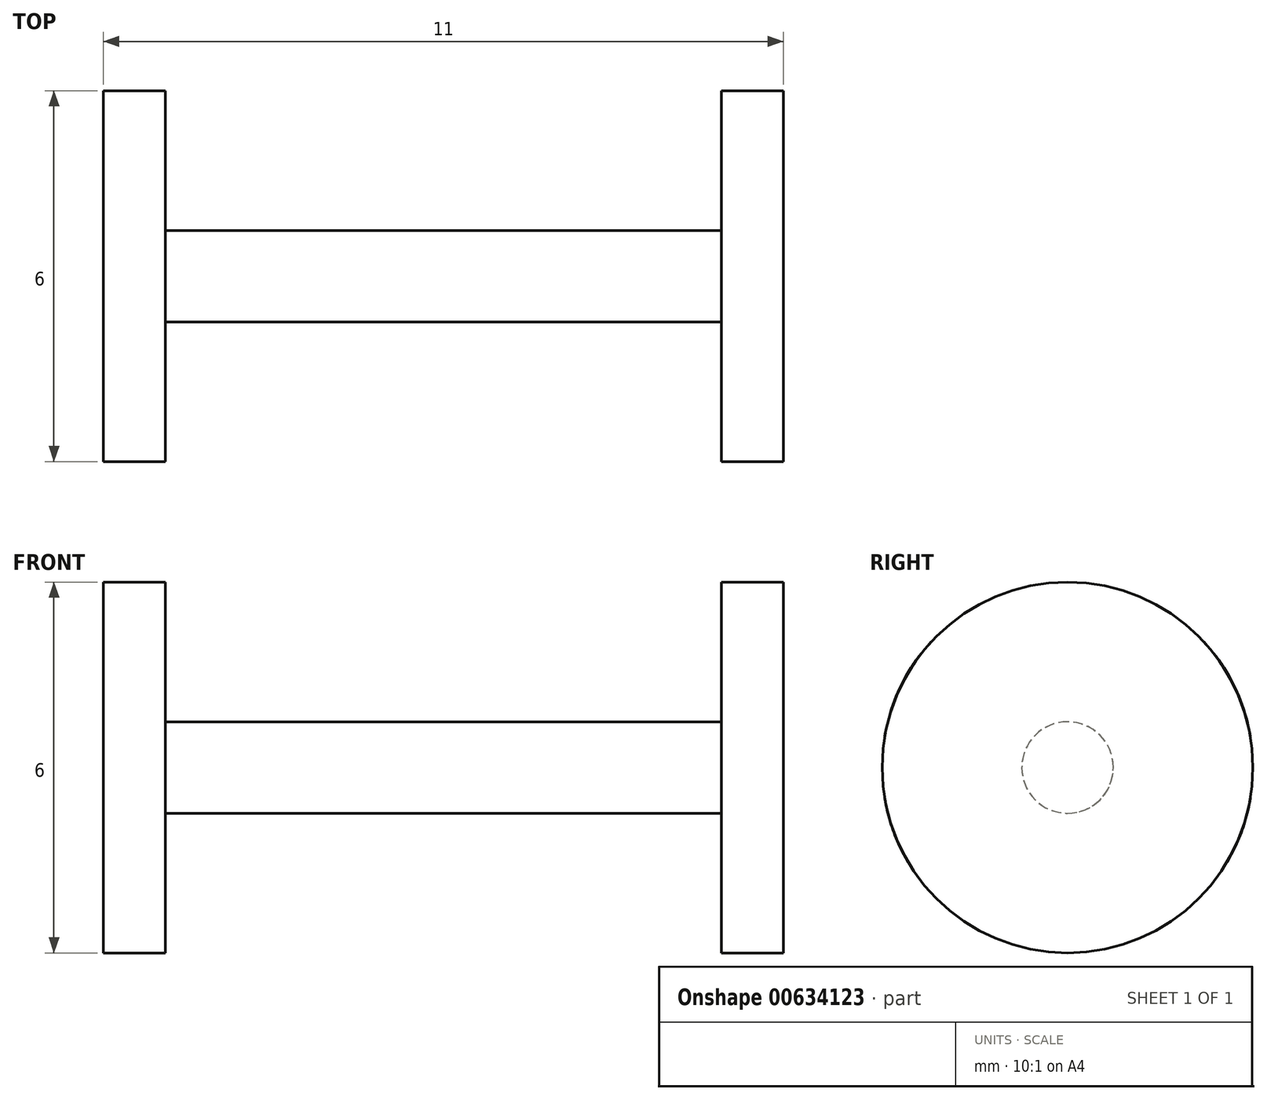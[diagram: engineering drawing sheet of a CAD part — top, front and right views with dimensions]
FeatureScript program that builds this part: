
annotation { "Feature Type Name" : "Feature", "Feature Type Description" : "" }
export const myFeature = defineFeature(function(context is Context, id is Id, definition is map)
    precondition{}
    {
        {
            var Q0;
            Q0=qCreatedBy(makeId("Front.planeOp"),FACE);
            var sketch = newSketch(context, id + "F0", { "sketchPlane" : qUnion([Q0])});
            skLineSegment(sketch, "E0.bottom", {"start": v(-15, 40) * mm, "end": v(15, 40) * mm});
            skLineSegment(sketch, "E0.top", {"start": v(-12, 0) * mm, "end": v(12, 0) * mm});
            skLineSegment(sketch, "E0.left", {"start": v(-15, 40) * mm, "end": v(-15, 37) * mm});
            skLineSegment(sketch, "E0.right", {"start": v(15, 37) * mm, "end": v(15, 3) * mm});
            skLineSegment(sketch, "E1.0", {"start": v(-15, 37) * mm, "end": v(3, 37) * mm});
            skLineSegment(sketch, "E1.1", {"start": v(-12, 6) * mm, "end": v(-12, 6) * mm});
            skLineSegment(sketch, "E1.2", {"start": v(-9, 3) * mm, "end": v(9, 3) * mm});
            skLineSegment(sketch, "E1.3", {"start": v(12, 29.6) * mm, "end": v(12, 6) * mm});
            skLineSegment(sketch, "E2.0", {"start": v(-15, 6) * mm, "end": v(-12, 6) * mm});
            skLineSegment(sketch, "E3", {"start": v(12, 40) * mm, "end": v(7.5, 40) * mm, "construction": true});
            skLineSegment(sketch, "E4", {"start": v(7, 34.8) * mm, "end": v(7, 40) * mm, "construction": true});
            skArc(sketch, "E5", {"start": v(7, 40) * mm, "mid": v(6.75, 29.6) * mm, "end": v(7.5, 39.98) * mm});
            skLineSegment(sketch, "E6.trimOffspring", {"start": v(-15, 6) * mm, "end": v(-15, 3) * mm});
            skPoint(sketch, "E7.orphan", {"position": v(5, 29.7) * mm});
            skPoint(sketch, "E8.visualSharp", {"position": v(15, 40) * mm});
            skArc(sketch, "E8.filletArc", {"start": v(15, 37) * mm, "mid": v(14.12, 39.12) * mm, "end": v(12, 40) * mm});
            skPoint(sketch, "E9.visualSharp", {"position": v(15, 0) * mm});
            skArc(sketch, "E9.filletArc", {"start": v(12, 0) * mm, "mid": v(14.12, 0.88) * mm, "end": v(15, 3) * mm});
            skArc(sketch, "E10.filletArc", {"start": v(9, 3) * mm, "mid": v(11.12, 3.88) * mm, "end": v(12, 6) * mm});
            skPoint(sketch, "E11.visualSharp", {"position": v(-12, 3) * mm});
            skArc(sketch, "E11.filletArc", {"start": v(-12, 6) * mm, "mid": v(-11.12, 3.88) * mm, "end": v(-9, 3) * mm});
            skPoint(sketch, "E12.visualSharp", {"position": v(-15, 0) * mm});
            skArc(sketch, "E12.filletArc", {"start": v(-15, 3) * mm, "mid": v(-14.12, 0.88) * mm, "end": v(-12, 0) * mm});
            skLineSegment(sketch, "E13.0", {"start": v(6.5, 34.8) * mm, "end": v(6.5, 39.8) * mm});
            skLineSegment(sketch, "E14.0", {"start": v(7.5, 34.8) * mm, "end": v(7.5, 40) * mm});
            skLineSegment(sketch, "E15", {"start": v(-15, 6) * mm, "end": v(-15, 16) * mm});
            skLineSegment(sketch, "E16", {"start": v(-15, 16) * mm, "end": v(-12, 16) * mm});
            skLineSegment(sketch, "E17", {"start": v(-12, 16) * mm, "end": v(-12, 6) * mm});
            skLineSegment(sketch, "E18", {"start": v(6.75, 29.6) * mm, "end": v(12, 29.6) * mm});
            skSolve(sketch);
        }
        {
            var Q0;
            Q0=qCreatedBy(makeId("Front.planeOp"),FACE);
            var sketch = newSketch(context, id + "F1", { "sketchPlane" : qUnion([Q0])});
            skLineSegment(sketch, "E19.1.1", {"start": v(7.5, 40) * mm, "end": v(-15, 40) * mm});
            skLineSegment(sketch, "E19.1.2", {"start": v(-15, 40) * mm, "end": v(-15, 37) * mm});
            skArc(sketch, "E19.2.8", {"start": v(-15, 3) * mm, "mid": v(-14.12, 0.88) * mm, "end": v(-12, 0) * mm, "construction": true});
            skLineSegment(sketch, "E19.2.9", {"start": v(-12, 0) * mm, "end": v(-5, 0) * mm});
            skLineSegment(sketch, "E19.2.13", {"start": v(17, 40) * mm, "end": v(8.5, 40) * mm});
            skLineSegment(sketch, "E19.3.0", {"start": v(-15, 18) * mm, "end": v(-15, 7.7) * mm});
            skPoint(sketch, "E20.2", {"position": v(6.5, 37.3) * mm});
            skPoint(sketch, "E21.orphan", {"position": v(6.5, 39.8) * mm});
            skPoint(sketch, "E19.0.2.end.orphan", {"position": v(7, 40) * mm});
            skPoint(sketch, "E22.orphan", {"position": v(12, 29.6) * mm});
            skPoint(sketch, "E23.orphan", {"position": v(7.5, 34.8) * mm});
            skPoint(sketch, "E20.0.start.orphan", {"position": v(6.5, 34.8) * mm});
            skLineSegment(sketch, "E24", {"start": v(-15, 37) * mm, "end": v(-15, 31) * mm});
            skLineSegment(sketch, "E25", {"start": v(0, 0) * mm, "end": v(0, 15) * mm, "construction": true});
            skLineSegment(sketch, "E26", {"start": v(7.5, 40) * mm, "end": v(7.5, 37.97) * mm});
            skLineSegment(sketch, "E27", {"start": v(8.5, 40) * mm, "end": v(8.5, 37.97) * mm});
            skLineSegment(sketch, "E28", {"start": v(15, 32.5) * mm, "end": v(8, 32.5) * mm, "construction": true});
            skPoint(sketch, "E29.orphan", {"position": v(7.6, 39) * mm});
            skLineSegment(sketch, "E30", {"start": v(8, 39) * mm, "end": v(8, 32.5) * mm, "construction": true});
            skPoint(sketch, "E19.3.3.end.orphan", {"position": v(-15, 16) * mm});
            skPoint(sketch, "E19.3.3.start.orphan", {"position": v(-12, 16) * mm});
            skLineSegment(sketch, "E31", {"start": v(-15, 3) * mm, "end": v(-15, 0) * mm});
            skLineSegment(sketch, "E32", {"start": v(-12, 0) * mm, "end": v(-15, 0) * mm});
            skLineSegment(sketch, "E33", {"start": v(-15, 40) * mm, "end": v(-15, 31) * mm, "construction": true});
            skLineSegment(sketch, "E34", {"start": v(-15, 40) * mm, "end": v(-15, 31) * mm});
            skLineSegment(sketch, "E35.trimOffspring", {"start": v(-15, 31) * mm, "end": v(-15, 26) * mm});
            skLineSegment(sketch, "E36.trimOffspring", {"start": v(-15, 29) * mm, "end": v(-15, 24) * mm});
            skPoint(sketch, "E37.orphan", {"position": v(12, 40) * mm});
            skPoint(sketch, "E38.orphan", {"position": v(12, 0) * mm});
            skLineSegment(sketch, "E39.0", {"start": v(13.1, 38) * mm, "end": v(13.1, 38) * mm});
            skLineSegment(sketch, "E40.1", {"start": v(-13, 2) * mm, "end": v(-11, 2) * mm, "construction": true});
            skLineSegment(sketch, "E41.0", {"start": v(-13, 38) * mm, "end": v(-13, 34) * mm});
            skArc(sketch, "E42", {"start": v(13.32, 33.87) * mm, "mid": v(11.56, 36.69) * mm, "end": v(8.5, 37.97) * mm});
            skLineSegment(sketch, "E43.0", {"start": v(29.42, 20) * mm, "end": v(-7, 20) * mm, "construction": true});
            skLineSegment(sketch, "E44.trimOffspring", {"start": v(-13, 0.17) * mm, "end": v(-13, 0) * mm});
            skArc(sketch, "E45.0", {"start": v(2.9, 38) * mm, "mid": v(3.81, 26.3) * mm, "end": v(15, 29.84) * mm});
            skLineSegment(sketch, "E46.trimOffspring", {"start": v(2.9, 38) * mm, "end": v(-13, 38) * mm});
            skLineSegment(sketch, "E47.trimOffspring", {"start": v(13.32, 33.87) * mm, "end": v(13.43, 31.7) * mm});
            skArc(sketch, "E48.trimOffspring", {"start": v(13.1, 38) * mm, "mid": v(13.1, 38) * mm, "end": v(13.1, 38) * mm});
            skArc(sketch, "E49.trimOffspring", {"start": v(7.5, 37.97) * mm, "mid": v(4.01, 28.73) * mm, "end": v(13.43, 31.7) * mm});
            skPoint(sketch, "E50.orphan", {"position": v(7.5, 39) * mm});
            skPoint(sketch, "E51.start.orphan", {"position": v(8.5, 39) * mm});
            skLineSegment(sketch, "E52.0", {"start": v(8, 0) * mm, "end": v(8, 13.5) * mm});
            skLineSegment(sketch, "E53.0", {"start": v(-5, 0) * mm, "end": v(-5, 13.5) * mm});
            skLineSegment(sketch, "E54.0", {"start": v(16.47, 12) * mm, "end": v(14.46, 12) * mm, "construction": true});
            skLineSegment(sketch, "E55.trimOffspring", {"start": v(12.84, 12) * mm, "end": v(10, 12) * mm});
            skLineSegment(sketch, "E56.0", {"start": v(1.5, 0) * mm, "end": v(1.5, 20) * mm, "construction": true});
            skLineSegment(sketch, "E57", {"start": v(1.5, 20) * mm, "end": v(-9.16, 15.5) * mm});
            skLineSegment(sketch, "E58", {"start": v(1.5, 20) * mm, "end": v(10.84, 15.5) * mm});
            skLineSegment(sketch, "E59.0", {"start": v(-9.16, 13.5) * mm, "end": v(-5, 13.5) * mm});
            skLineSegment(sketch, "E60", {"start": v(-9.16, 15.5) * mm, "end": v(-9.16, 13.5) * mm});
            skLineSegment(sketch, "E61", {"start": v(10.84, 15.5) * mm, "end": v(10.84, 13.5) * mm});
            skLineSegment(sketch, "E62.trimOffspring", {"start": v(8, 13.5) * mm, "end": v(10.84, 13.5) * mm});
            skLineSegment(sketch, "E63.trimOffspring", {"start": v(10, 2) * mm, "end": v(15, 2) * mm});
            skLineSegment(sketch, "E64.trimOffspring", {"start": v(8, 0) * mm, "end": v(17, 0) * mm});
            skLineSegment(sketch, "E65.0", {"start": v(10, 2) * mm, "end": v(10, 12) * mm});
            skLineSegment(sketch, "E66.0", {"start": v(1.55, 22.2) * mm, "end": v(-7, 18.58) * mm});
            skLineSegment(sketch, "E66.1", {"start": v(1.55, 22.2) * mm, "end": v(12.84, 16.75) * mm});
            skLineSegment(sketch, "E67.0", {"start": v(-11.16, 16.82) * mm, "end": v(-11.16, 15.5) * mm});
            skLineSegment(sketch, "E68.0", {"start": v(-13, 11.5) * mm, "end": v(-7, 11.5) * mm});
            skLineSegment(sketch, "E69", {"start": v(-11.16, 15.5) * mm, "end": v(-11.16, 13.5) * mm});
            skLineSegment(sketch, "E70.0", {"start": v(12.84, 16.75) * mm, "end": v(12.84, 12) * mm});
            skLineSegment(sketch, "E71.0", {"start": v(-13, 6.7) * mm, "end": v(-7, 6.7) * mm, "construction": true});
            skLineSegment(sketch, "E72.0", {"start": v(-15, 7.7) * mm, "end": v(-13, 7.7) * mm});
            skLineSegment(sketch, "E73.0", {"start": v(-15, 5.7) * mm, "end": v(-11, 5.7) * mm});
            skLineSegment(sketch, "E74.0", {"start": v(-15, 3.7) * mm, "end": v(-13, 3.7) * mm, "construction": true});
            skLineSegment(sketch, "E75.trimOffspring", {"start": v(-15, 5.7) * mm, "end": v(-15, 3) * mm});
            skLineSegment(sketch, "E76.trimOffspring", {"start": v(-13, 3.7) * mm, "end": v(-13, 2) * mm, "construction": true});
            skLineSegment(sketch, "E77.trimOffspring", {"start": v(-11, 5.7) * mm, "end": v(-11, 2) * mm});
            skLineSegment(sketch, "E78.0", {"start": v(-13, 13.5) * mm, "end": v(-11.16, 13.5) * mm});
            skLineSegment(sketch, "E79.trimOffspring", {"start": v(-9.16, 13.5) * mm, "end": v(-7, 13.5) * mm});
            skLineSegment(sketch, "E80.trimOffspring", {"start": v(-13, 11.5) * mm, "end": v(-13, 7.7) * mm});
            skLineSegment(sketch, "E81.0", {"start": v(-7, 11.5) * mm, "end": v(-7, 3.7) * mm});
            skLineSegment(sketch, "E82.trimOffspring", {"start": v(-11, 3.7) * mm, "end": v(-7, 3.7) * mm});
            skLineSegment(sketch, "E83.0", {"start": v(17, 40) * mm, "end": v(17, 0) * mm});
            skPoint(sketch, "E84.orphan", {"position": v(17.1, 0) * mm});
            skLineSegment(sketch, "E85.trimOffspring", {"start": v(15, 29.84) * mm, "end": v(15, 2) * mm});
            skPoint(sketch, "E86.start.orphan", {"position": v(15, 40) * mm});
            skLineSegment(sketch, "E87", {"start": v(-13, 13.5) * mm, "end": v(-13, 18) * mm});
            skLineSegment(sketch, "E88.trimOffspring", {"start": v(-15, 22) * mm, "end": v(-15, 21.16) * mm, "construction": true});
            skLineSegment(sketch, "E89.trimOffspring", {"start": v(-15, 22) * mm, "end": v(-15, 18) * mm});
            skPoint(sketch, "E90.start.orphan", {"position": v(-12, 28) * mm});
            skPoint(sketch, "E91.orphan", {"position": v(-12, 29) * mm});
            skLineSegment(sketch, "E92.0", {"start": v(-9, 26) * mm, "end": v(-11, 26) * mm});
            skLineSegment(sketch, "E93.0", {"start": v(-11, 24) * mm, "end": v(-13, 24) * mm});
            skLineSegment(sketch, "E94", {"start": v(-9, 20) * mm, "end": v(-9, 26) * mm});
            skLineSegment(sketch, "E95.0", {"start": v(-11, 20) * mm, "end": v(-11, 22) * mm});
            skLineSegment(sketch, "E96.trimOffspring", {"start": v(-11, 24) * mm, "end": v(-11, 26) * mm});
            skLineSegment(sketch, "E97.trimOffspring", {"start": v(-13, 28) * mm, "end": v(-13, 34) * mm});
            skLineSegment(sketch, "E98", {"start": v(-15, 22) * mm, "end": v(-11, 22) * mm});
            skLineSegment(sketch, "E99", {"start": v(-13, 24) * mm, "end": v(-15, 24) * mm});
            skLineSegment(sketch, "E100.0", {"start": v(-7, 18.58) * mm, "end": v(-7, 28) * mm});
            skLineSegment(sketch, "E101.0", {"start": v(-13, 18) * mm, "end": v(-8.36, 18) * mm});
            skLineSegment(sketch, "E102.trimOffspring", {"start": v(-8.36, 18) * mm, "end": v(-11.16, 16.82) * mm});
            skLineSegment(sketch, "E103.0", {"start": v(-11, 20) * mm, "end": v(-9, 20) * mm});
            skLineSegment(sketch, "E104.0", {"start": v(-7, 28) * mm, "end": v(-13, 28) * mm});
            skSolve(sketch);
        }
        {
            var Q0;
            Q0=qSketchRegion(id+"F1",true);
            extrude(context, id + "F2", {"entities" : qUnion([Q0]), "oppositeDirection" : true, "depth" : 1910 * mm, "offsetDistance" : 25 * mm});
        }
        {
            var Q0;
            Q0=makeQuery(id+"F1.imprint","IMPRINT",FACE,{"disambiguationData":[TD([[makeQuery(id+"F1.imprint","IMPRINT",EDGE,{"derivedFrom":sQuery(id+"F1.wireOp",EDGE,"E19.1.1")}),1.0]])]});
            var sketch = newSketch(context, id + "F3", { "sketchPlane" : qUnion([Q0])});
            skLineSegment(sketch, "E105.0", {"start": v(-13.5, 18) * mm, "end": v(-13.5, -0.51) * mm});
            skSolve(sketch);
        }
        {
            var Q0;
            Q0=makeQuery(id+"F3.imprint","IMPRINT",FACE,{"disambiguationData":[TD([[makeQuery(id+"F3.imprint","IMPRINT",EDGE,{"derivedFrom":makeQuery(id+"F1.imprint","IMPRINT",EDGE,{"derivedFrom":sQuery(id+"F1.wireOp",EDGE,"E19.1.1")})}),1.0]])]});
            var sketch = newSketch(context, id + "F4", { "sketchPlane" : qUnion([Q0])});
            skLineSegment(sketch, "E106.0", {"start": v(-17, 40) * mm, "end": v(-25.5, 40) * mm});
            skLineSegment(sketch, "E107.0", {"start": v(-49.1, 40) * mm, "end": v(-49.1, 18) * mm});
            skLineSegment(sketch, "E108.0", {"start": v(-17, 40) * mm, "end": v(-17, 18) * mm});
            skPoint(sketch, "E109.orphan", {"position": v(7.5, 40) * mm});
            skLineSegment(sketch, "E110.1", {"start": v(-19, 29.83) * mm, "end": v(-19, 20) * mm});
            skLineSegment(sketch, "E110.3", {"start": v(-47.1, 38) * mm, "end": v(-47.1, 20) * mm});
            skArc(sketch, "E111.0", {"start": v(7.5, 37.97) * mm, "mid": v(4.01, 28.73) * mm, "end": v(13.43, 31.7) * mm, "construction": true});
            skLineSegment(sketch, "E112.0", {"start": v(17, 40) * mm, "end": v(8.5, 40) * mm});
            skLineSegment(sketch, "E113.0", {"start": v(7.5, 40) * mm, "end": v(-15, 40) * mm});
            skLineSegment(sketch, "E114.0", {"start": v(-26.6, 40) * mm, "end": v(-26.6, 37.97) * mm});
            skLineSegment(sketch, "E115.0", {"start": v(-25.5, 40) * mm, "end": v(-25.5, 37.98) * mm});
            skLineSegment(sketch, "E116.0", {"start": v(-7, 18.58) * mm, "end": v(-7, 28) * mm});
            skLineSegment(sketch, "E117", {"start": v(-47.1, 23.29) * mm, "end": v(15, 23.29) * mm, "construction": true});
            skPoint(sketch, "E118.orphan", {"position": v(-7, 23.29) * mm});
            skLineSegment(sketch, "E119", {"start": v(8, 32.5) * mm, "end": v(2.5, 32.5) * mm});
            skLineSegment(sketch, "E120.0", {"start": v(8, 39) * mm, "end": v(8, 32.5) * mm});
            skLineSegment(sketch, "E120.1", {"start": v(17, 40) * mm, "end": v(17, 0) * mm});
            skLineSegment(sketch, "E121.trimOffspring", {"start": v(-17, 32.5) * mm, "end": v(-26, 32.5) * mm, "construction": true});
            skArc(sketch, "E122", {"start": v(-26.6, 37.97) * mm, "mid": v(-25.95, 27.01) * mm, "end": v(-25.5, 37.98) * mm});
            skArc(sketch, "E123.0", {"start": v(-31.1, 38) * mm, "mid": v(-30.2, 26.3) * mm, "end": v(-19, 29.83) * mm});
            skLineSegment(sketch, "E124.trimOffspring", {"start": v(-26.6, 40) * mm, "end": v(-49.1, 40) * mm});
            skLineSegment(sketch, "E125.trimOffspring", {"start": v(-26.6, 27.05) * mm, "end": v(-26.6, 20) * mm, "construction": true});
            skLineSegment(sketch, "E126.trimOffspring", {"start": v(-25.5, 27.04) * mm, "end": v(-25.5, 20) * mm, "construction": true});
            skLineSegment(sketch, "E127.trimOffspring", {"start": v(-31.1, 38) * mm, "end": v(-47.1, 38) * mm});
            skLineSegment(sketch, "E128.0", {"start": v(-49.1, 18) * mm, "end": v(-17, 18) * mm});
            skPoint(sketch, "E129.orphan", {"position": v(-8.36, 18) * mm});
            skPoint(sketch, "E130.orphan", {"position": v(-13, 18) * mm});
            skLineSegment(sketch, "E131.0", {"start": v(-47.1, 20) * mm, "end": v(-19, 20) * mm});
            skSolve(sketch);
        }
        {
            var Q0;
            Q0=makeQuery(id+"F1.imprint","IMPRINT",FACE,{"disambiguationData":[TD([[makeQuery(id+"F1.imprint","IMPRINT",EDGE,{"derivedFrom":sQuery(id+"F1.wireOp",EDGE,"E19.1.1")}),1.0]])]});
            var sketch = newSketch(context, id + "F5", { "sketchPlane" : qUnion([Q0])});
            skArc(sketch, "E132.0", {"start": v(7.5, 37.97) * mm, "mid": v(4.01, 28.73) * mm, "end": v(13.43, 31.7) * mm, "construction": true});
            skArc(sketch, "E132.1", {"start": v(13.32, 33.87) * mm, "mid": v(11.56, 36.69) * mm, "end": v(8.5, 37.97) * mm, "construction": true});
            skLineSegment(sketch, "E132.2", {"start": v(7.5, 40) * mm, "end": v(-15, 40) * mm});
            skArc(sketch, "E132.3", {"start": v(-26.6, 37.97) * mm, "mid": v(-25.95, 27.01) * mm, "end": v(-25.5, 37.98) * mm, "construction": true});
            skLineSegment(sketch, "E133.0", {"start": v(-15, 40) * mm, "end": v(-25.5, 40) * mm});
            skPoint(sketch, "E134.orphan", {"position": v(-26.6, 40) * mm});
            skLineSegment(sketch, "E135.0", {"start": v(7.5, 40) * mm, "end": v(7.5, 37.37) * mm});
            skLineSegment(sketch, "E135.1", {"start": v(8.5, 40) * mm, "end": v(8.5, 37.37) * mm});
            skLineSegment(sketch, "E135.2", {"start": v(-25.5, 40) * mm, "end": v(-25.5, 37.37) * mm});
            skLineSegment(sketch, "E135.3", {"start": v(-26.6, 40) * mm, "end": v(-26.6, 37.36) * mm});
            skPoint(sketch, "E135.4", {"position": v(-25.5, 38.99) * mm});
            skLineSegment(sketch, "E136", {"start": v(-49.1, 40) * mm, "end": v(-216.5, 40) * mm});
            skLineSegment(sketch, "E137.0", {"start": v(8.5, 41) * mm, "end": v(-216.5, 41) * mm});
            skLineSegment(sketch, "E138", {"start": v(8.5, 40) * mm, "end": v(8.5, 41) * mm});
            skLineSegment(sketch, "E139", {"start": v(-216.5, 41) * mm, "end": v(-216.5, 40) * mm, "construction": true});
            skArc(sketch, "E140.0", {"start": v(7.5, 37.37) * mm, "mid": v(4.47, 29.12) * mm, "end": v(12.84, 31.8) * mm});
            skArc(sketch, "E141.0", {"start": v(12.74, 33.72) * mm, "mid": v(11.2, 36.21) * mm, "end": v(8.5, 37.37) * mm});
            skArc(sketch, "E142", {"start": v(12.74, 33.72) * mm, "mid": v(12.88, 32.76) * mm, "end": v(12.84, 31.8) * mm});
            skPoint(sketch, "E143.orphan", {"position": v(7.5, 37.97) * mm});
            skPoint(sketch, "E144.orphan", {"position": v(8.5, 37.97) * mm});
            skArc(sketch, "E145.0", {"start": v(-26.6, 37.36) * mm, "mid": v(-25.95, 27.61) * mm, "end": v(-25.5, 37.37) * mm});
            skPoint(sketch, "E146.orphan", {"position": v(-26.6, 37.97) * mm});
            skPoint(sketch, "E147.orphan", {"position": v(-25.5, 37.98) * mm});
            skLineSegment(sketch, "E148.trimOffspring", {"start": v(-26.6, 40) * mm, "end": v(-49.1, 40) * mm});
            skSolve(sketch);
        }
        {
            var Q0;
            {var subQ7=sQuery(id+"F5.wireOp",EDGE,"E132.2");Q0=makeQuery(id+"F5.imprint","IMPRINT",FACE,{"disambiguationData":[TD([[makeQuery(id+"F5.imprint","IMPRINT",EDGE,{"derivedFrom":subQ7}),1.0]])]});}
            var sketch = newSketch(context, id + "F6", { "sketchPlane" : qUnion([Q0])});
            skLineSegment(sketch, "E149.0", {"start": v(-13, 11.5) * mm, "end": v(-7, 11.5) * mm});
            skLineSegment(sketch, "E149.1", {"start": v(-7, 11.5) * mm, "end": v(-7, 3.7) * mm});
            skLineSegment(sketch, "E149.2", {"start": v(-11, 3.7) * mm, "end": v(-7, 3.7) * mm});
            skLineSegment(sketch, "E149.3", {"start": v(-11, 5.7) * mm, "end": v(-11, 3.7) * mm});
            skLineSegment(sketch, "E149.4", {"start": v(-15, 5.7) * mm, "end": v(-11, 5.7) * mm});
            skLineSegment(sketch, "E149.5", {"start": v(-15, 7.7) * mm, "end": v(-13, 7.7) * mm});
            skLineSegment(sketch, "E149.6", {"start": v(-13, 11.5) * mm, "end": v(-13, 7.7) * mm});
            skPoint(sketch, "E150.orphan", {"position": v(-11, 2) * mm});
            skLineSegment(sketch, "E151.0", {"start": v(-15, 18) * mm, "end": v(-15, 7.7) * mm});
            skLineSegment(sketch, "E151.1", {"start": v(-15, 3) * mm, "end": v(-15, 0) * mm});
            skLineSegment(sketch, "E151.2", {"start": v(-15, 5.7) * mm, "end": v(-15, 3) * mm});
            skLineSegment(sketch, "E152.0", {"start": v(-17, 18) * mm, "end": v(-17, 15.63) * mm});
            skLineSegment(sketch, "E153.0", {"start": v(-17, 3) * mm, "end": v(-17, 0) * mm});
            skLineSegment(sketch, "E154", {"start": v(-17, 18) * mm, "end": v(-15, 18) * mm});
            skLineSegment(sketch, "E155", {"start": v(-17, 0) * mm, "end": v(-15, 0) * mm});
            skLineSegment(sketch, "E156", {"start": v(-17, 3) * mm, "end": v(-26.75, 3) * mm});
            skLineSegment(sketch, "E157", {"start": v(-26.75, 3) * mm, "end": v(-26.75, 15.63) * mm});
            skLineSegment(sketch, "E158", {"start": v(-26.75, 15.63) * mm, "end": v(-17, 15.63) * mm});
            skSolve(sketch);
        }
        {
            var Q0;
            Q0=makeQuery(id+"F2.opExtrude","CAP_FACE",FACE,{"disambiguationData":[OSD([sQuery(id+"F1.wireOp",EDGE,"E19.1.1"),sQuery(id+"F1.wireOp",EDGE,"E19.2.9"),sQuery(id+"F1.wireOp",EDGE,"E19.2.13"),sQuery(id+"F1.wireOp",EDGE,"E19.3.0"),sQuery(id+"F1.wireOp",EDGE,"E26"),sQuery(id+"F1.wireOp",EDGE,"E27"),sQuery(id+"F1.wireOp",EDGE,"E31"),sQuery(id+"F1.wireOp",EDGE,"E32"),sQuery(id+"F1.wireOp",EDGE,"E34"),sQuery(id+"F1.wireOp",EDGE,"E35.trimOffspring"),sQuery(id+"F1.wireOp",EDGE,"E36.trimOffspring"),sQuery(id+"F1.wireOp",EDGE,"E39.0"),sQuery(id+"F1.wireOp",EDGE,"E39.0"),sQuery(id+"F1.wireOp",EDGE,"E41.0"),sQuery(id+"F1.wireOp",EDGE,"E42"),sQuery(id+"F1.wireOp",EDGE,"E45.0"),sQuery(id+"F1.wireOp",EDGE,"E46.trimOffspring"),sQuery(id+"F1.wireOp",EDGE,"E47.trimOffspring"),sQuery(id+"F1.wireOp",EDGE,"E48.trimOffspring"),sQuery(id+"F1.wireOp",EDGE,"E49.trimOffspring"),sQuery(id+"F1.wireOp",EDGE,"E52.0"),sQuery(id+"F1.wireOp",EDGE,"E53.0"),sQuery(id+"F1.wireOp",EDGE,"E55.trimOffspring"),sQuery(id+"F1.wireOp",EDGE,"E57"),sQuery(id+"F1.wireOp",EDGE,"E58"),sQuery(id+"F1.wireOp",EDGE,"E59.0"),sQuery(id+"F1.wireOp",EDGE,"E60"),sQuery(id+"F1.wireOp",EDGE,"E61"),sQuery(id+"F1.wireOp",EDGE,"E62.trimOffspring"),sQuery(id+"F1.wireOp",EDGE,"E63.trimOffspring"),sQuery(id+"F1.wireOp",EDGE,"E64.trimOffspring"),sQuery(id+"F1.wireOp",EDGE,"E65.0"),sQuery(id+"F1.wireOp",EDGE,"E66.0"),sQuery(id+"F1.wireOp",EDGE,"E66.1"),sQuery(id+"F1.wireOp",EDGE,"E67.0"),sQuery(id+"F1.wireOp",EDGE,"E68.0"),sQuery(id+"F1.wireOp",EDGE,"E69"),sQuery(id+"F1.wireOp",EDGE,"E70.0"),sQuery(id+"F1.wireOp",EDGE,"E72.0"),sQuery(id+"F1.wireOp",EDGE,"E73.0"),sQuery(id+"F1.wireOp",EDGE,"E75.trimOffspring"),sQuery(id+"F1.wireOp",EDGE,"E77.trimOffspring"),sQuery(id+"F1.wireOp",EDGE,"E78.0"),sQuery(id+"F1.wireOp",EDGE,"E79.trimOffspring"),sQuery(id+"F1.wireOp",EDGE,"E80.trimOffspring"),sQuery(id+"F1.wireOp",EDGE,"E81.0"),sQuery(id+"F1.wireOp",EDGE,"E82.trimOffspring"),sQuery(id+"F1.wireOp",EDGE,"E83.0"),sQuery(id+"F1.wireOp",EDGE,"E85.trimOffspring"),sQuery(id+"F1.wireOp",EDGE,"E87"),sQuery(id+"F1.wireOp",EDGE,"E89.trimOffspring"),sQuery(id+"F1.wireOp",EDGE,"E92.0"),sQuery(id+"F1.wireOp",EDGE,"E93.0"),sQuery(id+"F1.wireOp",EDGE,"E94"),sQuery(id+"F1.wireOp",EDGE,"E95.0"),sQuery(id+"F1.wireOp",EDGE,"E96.trimOffspring"),sQuery(id+"F1.wireOp",EDGE,"E97.trimOffspring"),sQuery(id+"F1.wireOp",EDGE,"E98"),sQuery(id+"F1.wireOp",EDGE,"E99"),sQuery(id+"F1.wireOp",EDGE,"E100.0"),sQuery(id+"F1.wireOp",EDGE,"E101.0"),sQuery(id+"F1.wireOp",EDGE,"E102.trimOffspring"),sQuery(id+"F1.wireOp",EDGE,"E103.0"),sQuery(id+"F1.wireOp",EDGE,"E104.0")])],"isStart":true});
            var sketch = newSketch(context, id + "F7", { "sketchPlane" : qUnion([Q0])});
            skLineSegment(sketch, "E159.0", {"start": v(-11, 24) * mm, "end": v(-15, 24) * mm, "construction": true});
            skLineSegment(sketch, "E159.1", {"start": v(-15, 22) * mm, "end": v(-11, 22) * mm, "construction": true});
            skLineSegment(sketch, "E159.2", {"start": v(-10.5, 20) * mm, "end": v(-9.5, 20) * mm});
            skLineSegment(sketch, "E159.3", {"start": v(-9, 20) * mm, "end": v(-9, 26) * mm, "construction": true});
            skLineSegment(sketch, "E159.4", {"start": v(-9.5, 26) * mm, "end": v(-10.5, 26) * mm});
            skLineSegment(sketch, "E159.5", {"start": v(-11, 24) * mm, "end": v(-11, 26) * mm, "construction": true});
            skPoint(sketch, "E159.6", {"position": v(-11, 21) * mm});
            skLineSegment(sketch, "E160.0", {"start": v(-9.5, 20) * mm, "end": v(-9.5, 26) * mm});
            skLineSegment(sketch, "E161.0", {"start": v(-10.5, 20) * mm, "end": v(-10.5, 22.5) * mm});
            skLineSegment(sketch, "E162", {"start": v(-9.5, 23) * mm, "end": v(-16.2, 23) * mm, "construction": true});
            skLineSegment(sketch, "E163.0", {"start": v(-10.5, 23.5) * mm, "end": v(-16.2, 23.5) * mm});
            skLineSegment(sketch, "E164.0", {"start": v(-10.5, 22.5) * mm, "end": v(-16.2, 22.5) * mm});
            skLineSegment(sketch, "E165.trimOffspring", {"start": v(-10.5, 23.5) * mm, "end": v(-10.5, 26) * mm});
            skLineSegment(sketch, "E166.0", {"start": v(-15, 40) * mm, "end": v(-15, 24) * mm});
            skLineSegment(sketch, "E167.MirrorCS", {"start": v(-19.5, 23.5) * mm, "end": v(-13.8, 23.5) * mm});
            skLineSegment(sketch, "E168.MirrorCS", {"start": v(-20.5, 23) * mm, "end": v(-13.8, 23) * mm, "construction": true});
            skLineSegment(sketch, "E169.MirrorCS", {"start": v(-19.5, 22.5) * mm, "end": v(-13.8, 22.5) * mm});
            skLineSegment(sketch, "E170.MirrorCS", {"start": v(-20.5, 20) * mm, "end": v(-20.5, 26) * mm});
            skLineSegment(sketch, "E171.MirrorCS", {"start": v(-19.5, 23.5) * mm, "end": v(-19.5, 26) * mm});
            skLineSegment(sketch, "E172.MirrorCS", {"start": v(-19.5, 20) * mm, "end": v(-19.5, 22.5) * mm});
            skLineSegment(sketch, "E173.MirrorCS", {"start": v(-20.5, 26) * mm, "end": v(-19.5, 26) * mm});
            skLineSegment(sketch, "E174.MirrorCS", {"start": v(-19.5, 20) * mm, "end": v(-20.5, 20) * mm});
            skPoint(sketch, "E175.orphan", {"position": v(-19, 26) * mm});
            skPoint(sketch, "E176.orphan", {"position": v(-19, 20) * mm});
            skPoint(sketch, "E177.orphan", {"position": v(-11, 20) * mm});
            skSolve(sketch);
        }
        {
            var Q0;
            Q0 = qSketchRegion(id + "F7", true);
            extrude(context, id + "F8", {"entities" : qUnion([Q0]), "oppositeDirection" : true, "depth" : 10 * mm, "offsetDistance" : 25 * mm});
        }
        {
            var Q0;
            Q0=makeQuery(id+"F3.imprint","IMPRINT",FACE,{"disambiguationData":[TD([[makeQuery(id+"F3.imprint","IMPRINT",EDGE,{"derivedFrom":makeQuery(id+"F1.imprint","IMPRINT",EDGE,{"derivedFrom":sQuery(id+"F1.wireOp",EDGE,"E19.1.1")})}),1.0]])]});
            var sketch = newSketch(context, id + "F9", { "sketchPlane" : qUnion([Q0])});
            skLineSegment(sketch, "E178.0.0", {"start": v(-15, 0) * mm, "end": v(-13, 0) * mm});
            skLineSegment(sketch, "E178.0.1", {"start": v(-13, 0) * mm, "end": v(-12, 0) * mm});
            skLineSegment(sketch, "E178.0.2", {"start": v(-12, 0) * mm, "end": v(-5, 0) * mm});
            skLineSegment(sketch, "E178.0.3", {"start": v(-5, 0) * mm, "end": v(-5, 13.5) * mm});
            skLineSegment(sketch, "E178.0.4", {"start": v(-5, 13.5) * mm, "end": v(-7, 13.5) * mm});
            skLineSegment(sketch, "E178.0.5", {"start": v(-7, 13.5) * mm, "end": v(-9.16, 13.5) * mm});
            skLineSegment(sketch, "E178.0.6", {"start": v(-9.16, 13.5) * mm, "end": v(-9.16, 15.5) * mm});
            skLineSegment(sketch, "E178.0.7", {"start": v(-9.16, 15.5) * mm, "end": v(1.5, 20) * mm});
            skLineSegment(sketch, "E178.0.8", {"start": v(1.5, 20) * mm, "end": v(10.84, 15.5) * mm});
            skLineSegment(sketch, "E178.0.9", {"start": v(10.84, 15.5) * mm, "end": v(10.84, 13.5) * mm});
            skLineSegment(sketch, "E178.0.10", {"start": v(10.84, 13.5) * mm, "end": v(8, 13.5) * mm});
            skLineSegment(sketch, "E178.0.11", {"start": v(8, 13.5) * mm, "end": v(8, 0) * mm});
            skLineSegment(sketch, "E178.0.12", {"start": v(8, 0) * mm, "end": v(17, 0) * mm});
            skLineSegment(sketch, "E178.0.13", {"start": v(17, 0) * mm, "end": v(17, 40) * mm});
            skLineSegment(sketch, "E178.0.14", {"start": v(17, 40) * mm, "end": v(8.5, 40) * mm});
            skLineSegment(sketch, "E178.0.15", {"start": v(8.5, 40) * mm, "end": v(8.5, 37.97) * mm});
            skArc(sketch, "E178.0.16", {"start": v(8.5, 37.97) * mm, "mid": v(11.56, 36.69) * mm, "end": v(13.32, 33.87) * mm});
            skLineSegment(sketch, "E178.0.17", {"start": v(13.32, 33.87) * mm, "end": v(13.43, 31.7) * mm});
            skArc(sketch, "E178.0.18", {"start": v(13.43, 31.7) * mm, "mid": v(4.01, 28.73) * mm, "end": v(7.5, 37.97) * mm});
            skLineSegment(sketch, "E178.0.19", {"start": v(7.5, 37.97) * mm, "end": v(7.5, 40) * mm});
            skLineSegment(sketch, "E178.0.20", {"start": v(7.5, 40) * mm, "end": v(-15, 40) * mm});
            skLineSegment(sketch, "E178.0.21", {"start": v(-15, 40) * mm, "end": v(-15, 31) * mm});
            skLineSegment(sketch, "E178.0.22", {"start": v(-15, 31) * mm, "end": v(-15, 29) * mm});
            skLineSegment(sketch, "E178.0.23", {"start": v(-15, 29) * mm, "end": v(-15, 24) * mm});
            skLineSegment(sketch, "E178.0.24", {"start": v(-15, 24) * mm, "end": v(-13, 24) * mm});
            skLineSegment(sketch, "E178.0.25", {"start": v(-13, 24) * mm, "end": v(-11, 24) * mm});
            skLineSegment(sketch, "E178.0.26", {"start": v(-11, 24) * mm, "end": v(-11, 26) * mm});
            skLineSegment(sketch, "E178.0.27", {"start": v(-11, 26) * mm, "end": v(-9, 26) * mm});
            skLineSegment(sketch, "E178.0.28", {"start": v(-9, 26) * mm, "end": v(-9, 20) * mm});
            skLineSegment(sketch, "E178.0.29", {"start": v(-9, 20) * mm, "end": v(-11, 20) * mm});
            skLineSegment(sketch, "E178.0.30", {"start": v(-11, 20) * mm, "end": v(-11, 22) * mm});
            skLineSegment(sketch, "E178.0.31", {"start": v(-11, 22) * mm, "end": v(-15, 22) * mm});
            skLineSegment(sketch, "E178.0.32", {"start": v(-15, 22) * mm, "end": v(-15, 18) * mm});
            skLineSegment(sketch, "E178.0.33", {"start": v(-15, 18) * mm, "end": v(-15, 7.7) * mm});
            skLineSegment(sketch, "E178.0.34", {"start": v(-15, 7.7) * mm, "end": v(-13, 7.7) * mm});
            skLineSegment(sketch, "E178.0.35", {"start": v(-13, 7.7) * mm, "end": v(-13, 11.5) * mm});
            skLineSegment(sketch, "E178.0.36", {"start": v(-13, 11.5) * mm, "end": v(-7, 11.5) * mm});
            skLineSegment(sketch, "E178.0.37", {"start": v(-7, 11.5) * mm, "end": v(-7, 3.7) * mm});
            skLineSegment(sketch, "E178.0.38", {"start": v(-7, 3.7) * mm, "end": v(-11, 3.7) * mm});
            skLineSegment(sketch, "E178.0.39", {"start": v(-11, 3.7) * mm, "end": v(-11, 5.7) * mm});
            skLineSegment(sketch, "E178.0.40", {"start": v(-11, 5.7) * mm, "end": v(-15, 5.7) * mm});
            skLineSegment(sketch, "E178.0.41", {"start": v(-15, 5.7) * mm, "end": v(-15, 3) * mm});
            skLineSegment(sketch, "E178.0.42", {"start": v(-15, 3) * mm, "end": v(-15, 0) * mm});
            skLineSegment(sketch, "E179.0.0", {"start": v(12.84, 16.75) * mm, "end": v(12.84, 12) * mm});
            skLineSegment(sketch, "E179.0.1", {"start": v(12.84, 12) * mm, "end": v(10, 12) * mm});
            skLineSegment(sketch, "E179.0.2", {"start": v(10, 12) * mm, "end": v(10, 2) * mm});
            skLineSegment(sketch, "E179.0.3", {"start": v(10, 2) * mm, "end": v(15, 2) * mm});
            skLineSegment(sketch, "E179.0.4", {"start": v(15, 2) * mm, "end": v(15, 29.84) * mm});
            skArc(sketch, "E179.0.5", {"start": v(15, 29.84) * mm, "mid": v(3.81, 26.3) * mm, "end": v(2.9, 38) * mm});
            skLineSegment(sketch, "E179.0.6", {"start": v(2.9, 38) * mm, "end": v(-13, 38) * mm});
            skLineSegment(sketch, "E179.0.7", {"start": v(-13, 38) * mm, "end": v(-13, 34) * mm});
            skLineSegment(sketch, "E179.0.8", {"start": v(-13, 34) * mm, "end": v(-13, 28) * mm});
            skLineSegment(sketch, "E179.0.9", {"start": v(-13, 28) * mm, "end": v(-7, 28) * mm});
            skLineSegment(sketch, "E179.0.10", {"start": v(-7, 28) * mm, "end": v(-7, 18.58) * mm});
            skLineSegment(sketch, "E179.0.11", {"start": v(-7, 18.58) * mm, "end": v(1.55, 22.2) * mm});
            skLineSegment(sketch, "E179.0.12", {"start": v(1.55, 22.2) * mm, "end": v(12.84, 16.75) * mm});
            skLineSegment(sketch, "E180.0.0", {"start": v(-13, 18) * mm, "end": v(-13, 13.5) * mm});
            skLineSegment(sketch, "E180.0.1", {"start": v(-13, 13.5) * mm, "end": v(-11.16, 13.5) * mm});
            skLineSegment(sketch, "E180.0.2", {"start": v(-11.16, 13.5) * mm, "end": v(-11.16, 15.5) * mm});
            skLineSegment(sketch, "E180.0.3", {"start": v(-11.16, 15.5) * mm, "end": v(-11.16, 16.82) * mm});
            skLineSegment(sketch, "E180.0.4", {"start": v(-11.16, 16.82) * mm, "end": v(-8.36, 18) * mm});
            skLineSegment(sketch, "E180.0.5", {"start": v(-8.36, 18) * mm, "end": v(-13, 18) * mm});
            skSolve(sketch);
        }
        {
            var Q0;
            Q0 = qSketchRegion(id + "F9", true);
            extrude(context, id + "F10", {"entities" : qUnion([Q0]), "operationType" : NewBodyOperationType.REMOVE, "oppositeDirection" : true, "depth" : 2071 * mm, "offsetDistance" : 25 * mm});
        }
        {
            var Q0;
            Q0=makeQuery(id+"F8.opExtrude","SWEPT_FACE",FACE,{"disambiguationData":[OSD([sQuery(id+"F7.wireOp",EDGE,"E160.0")])]});
            var sketch = newSketch(context, id + "F11", { "sketchPlane" : qUnion([Q0])});
            skLineSegment(sketch, "E181", {"start": v(5, 20) * mm, "end": v(5, 26) * mm, "construction": true});
            skLineSegment(sketch, "E182", {"start": v(0, 23) * mm, "end": v(10, 23) * mm, "construction": true});
            skCircle(sketch, "E183", {"center": v(5, 23) * mm, "radius": 3 * mm});
            skSolve(sketch);
        }
        {
            var Q0;
            {var subQ1=sQuery(id+"F7.wireOp",EDGE,"E160.0");var subQ6=makeQuery(id+"F8.opExtrude","CAP_EDGE",EDGE,{"disambiguationData":[OSD([subQ1])],"isStart":false});Q0=makeQuery(id+"F11.imprint","IMPRINT",FACE,{"disambiguationData":[TD([[makeQuery(id+"F11.imprint","IMPRINT",EDGE,{"derivedFrom":subQ6}),1.0]])]});}
            var Q1;
            {var subQ1=sQuery(id+"F7.wireOp",EDGE,"E160.0");var subQ6=makeQuery(id+"F8.opExtrude","CAP_EDGE",EDGE,{"disambiguationData":[OSD([subQ1])],"isStart":true});Q1=makeQuery(id+"F11.imprint","IMPRINT",FACE,{"disambiguationData":[TD([[makeQuery(id+"F11.imprint","IMPRINT",EDGE,{"derivedFrom":subQ6}),-1.0]])]});}
            extrude(context, id + "F12", {"entities" : qUnion([Q0, Q1]), "operationType" : NewBodyOperationType.REMOVE, "oppositeDirection" : true, "depth" : 25 * mm, "offsetDistance" : 25 * mm});
        }
        {
            var Q0;
            Q0=qCreatedBy(makeId("Front.planeOp"),FACE);
            var sketch = newSketch(context, id + "F13", { "sketchPlane" : qUnion([Q0])});
            skLineSegment(sketch, "E184.bottom", {"start": v(-19.5, 25.03) * mm, "end": v(-10.5, 25.03) * mm});
            skLineSegment(sketch, "E184.top", {"start": v(-19.5, 21.47) * mm, "end": v(-10.5, 21.47) * mm});
            skLineSegment(sketch, "E184.left", {"start": v(-19.5, 25.03) * mm, "end": v(-19.5, 21.47) * mm});
            skLineSegment(sketch, "E184.right", {"start": v(-10.5, 25.03) * mm, "end": v(-10.5, 21.47) * mm});
            skSolve(sketch);
        }
        {
            var Q0;
            Q0 = qSketchRegion(id + "F13", true);
            extrude(context, id + "F14", {"entities" : qUnion([Q0]), "operationType" : NewBodyOperationType.REMOVE, "oppositeDirection" : true, "depth" : 12.65 * mm, "offsetDistance" : 25 * mm});
        }
        {
            var Q0;
            Q0=makeQuery(id+"F8.opExtrude","SWEPT_FACE",FACE,{"disambiguationData":[OSD([sQuery(id+"F7.wireOp",EDGE,"E161.0")])]});
            var sketch = newSketch(context, id + "F15", { "sketchPlane" : qUnion([Q0])});
            skCircle(sketch, "E185", {"center": v(-5, 23) * mm, "radius": 0.74 * mm});
            skSolve(sketch);
        }
        {
            var Q0;
            Q0 = qSketchRegion(id + "F15", true);
            var Q1;
            Q1=makeQuery(id+"F8.opExtrude","SWEPT_FACE",FACE,{"disambiguationData":[OSD([sQuery(id+"F7.wireOp",EDGE,"E171.MirrorCS")])]});
            extrude(context, id + "F16", {"entities" : qUnion([Q0]), "endBound" : BoundingType.UP_TO_SURFACE, "depth" : 25 * mm, "endBoundEntityFace" : qUnion([Q1]), "offsetDistance" : 25 * mm});
        }
    });
